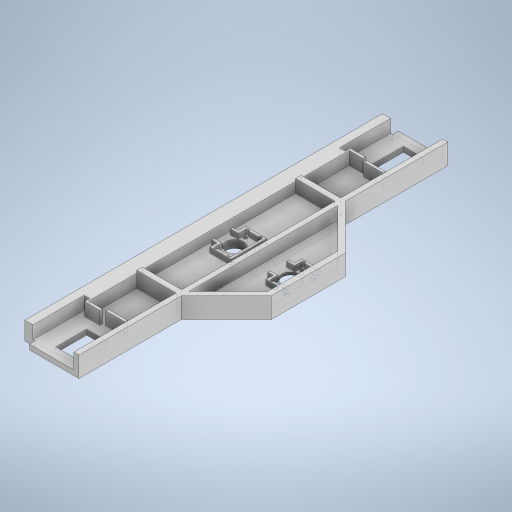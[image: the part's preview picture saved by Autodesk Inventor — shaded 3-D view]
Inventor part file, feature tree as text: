
AUTODESK INVENTOR PART (.ipt)
format: ipt  version: 2024 (Build 280153000, 153)  size: 558,080 bytes
history: native  units: mm
features: sketch x13, extrude x12, projected_geometry x3, chamfer x2, other x1
ambient origin geometry x8: Origin, YZ Plane, XZ Plane, XY Plane, X Axis, Y Axis, Z Axis, Center Point
bodies: Body1 (feature_tree)
feature tree (31):
  other  "Твердое тело1"
  extrude  "Выдавливание1"  Depth=722.0mm
  extrude  "Выдавливание2"  Depth=21.0mm
  extrude  "Выдавливание3"  Depth=60.0mm
  extrude  "Выдавливание4"  Depth=40.0mm
  extrude  "Выдавливание5"  Depth=10.0mm TaperAngle=0.0deg
  extrude  "Выдавливание6"  Depth=10.0mm
  extrude  "Выдавливание7"  Depth=500.0mm
  extrude  "Выдавливание8"  Depth=111.0mm
  chamfer  "Фаска1"  Distance=25.0mm
  extrude  "Выдавливание9"  Depth=700.0mm
  extrude  "Выдавливание11"  Depth=11.0mm
  sketch  "Sketch13"  dims[d0=87.0mm d1=722.0mm]
  chamfer  "Chamfer2"  Distance=35.0mm
  extrude  "Extrusion12"  Depth=20.0mm
  extrude  "Extrusion13"  Depth=10.0mm
  sketch  "Эскиз1"
  sketch  "Эскиз2"
  sketch  "Эскиз3"
  sketch  "Эскиз4"
  sketch  "Эскиз6"
  sketch  "Эскиз7"
  sketch  "Эскиз8"
  sketch  "Эскиз9"
  projected_geometry  "Спроецированная петля1"
  sketch  "Эскиз10"
  projected_geometry  "Спроецированная петля2"
  projected_geometry  "Спроецированная петля3"
  sketch  "Эскиз12"
  sketch  "Sketch14"  dims[d2=10.0mm d3=0.0mm d4=21.0mm]
  sketch  "Sketch15"  dims[d5=16.0mm d6=60.0mm d7=40.0mm d8=10.0mm d9=0.0mm d10=10.0mm d12=500.0mm d13=111.0mm d14=25.0mm d15=0.0mm d16=700.0mm d17=11.0mm d18=35.0mm d19=0.0mm d20=20.0mm d22=10.0mm d23=40.0mm d24=0.0mm d25=200.0mm d26=200.0mm d27=5.0mm d28=0.0mm d29=42.0mm d30=70.0mm d31=326.0mm d32=5.0mm d33=10.5mm d34=10.0mm d35=0.0mm d36=4.25mm d37=4.25mm d38=4.25mm d39=4.25mm d40=19.0mm d41=34.0mm d42=20.0mm d43=0.0mm d44=12.0mm d45=2.0mm d46=45.0deg d47=5.0mm d48=5.0mm d49=19.0mm d50=19.0mm d51=2.0mm d52=0.0mm d56=10.0mm d57=20.0mm d58=5.0mm d59=25.0mm d60=0.0mm d61=42.0mm d62=70.0mm d63=5.0mm d64=10.5mm d65=5.0mm d66=5.0mm d67=19.0mm d68=19.0mm d69=19.0mm d70=34.0mm d71=88.0mm d72=2.0mm d73=45.0deg d75=11.0mm d76=40.0mm d77=0.0mm d78=11.0mm d79=11.0mm d80=2.0mm d81=0.0mm]
